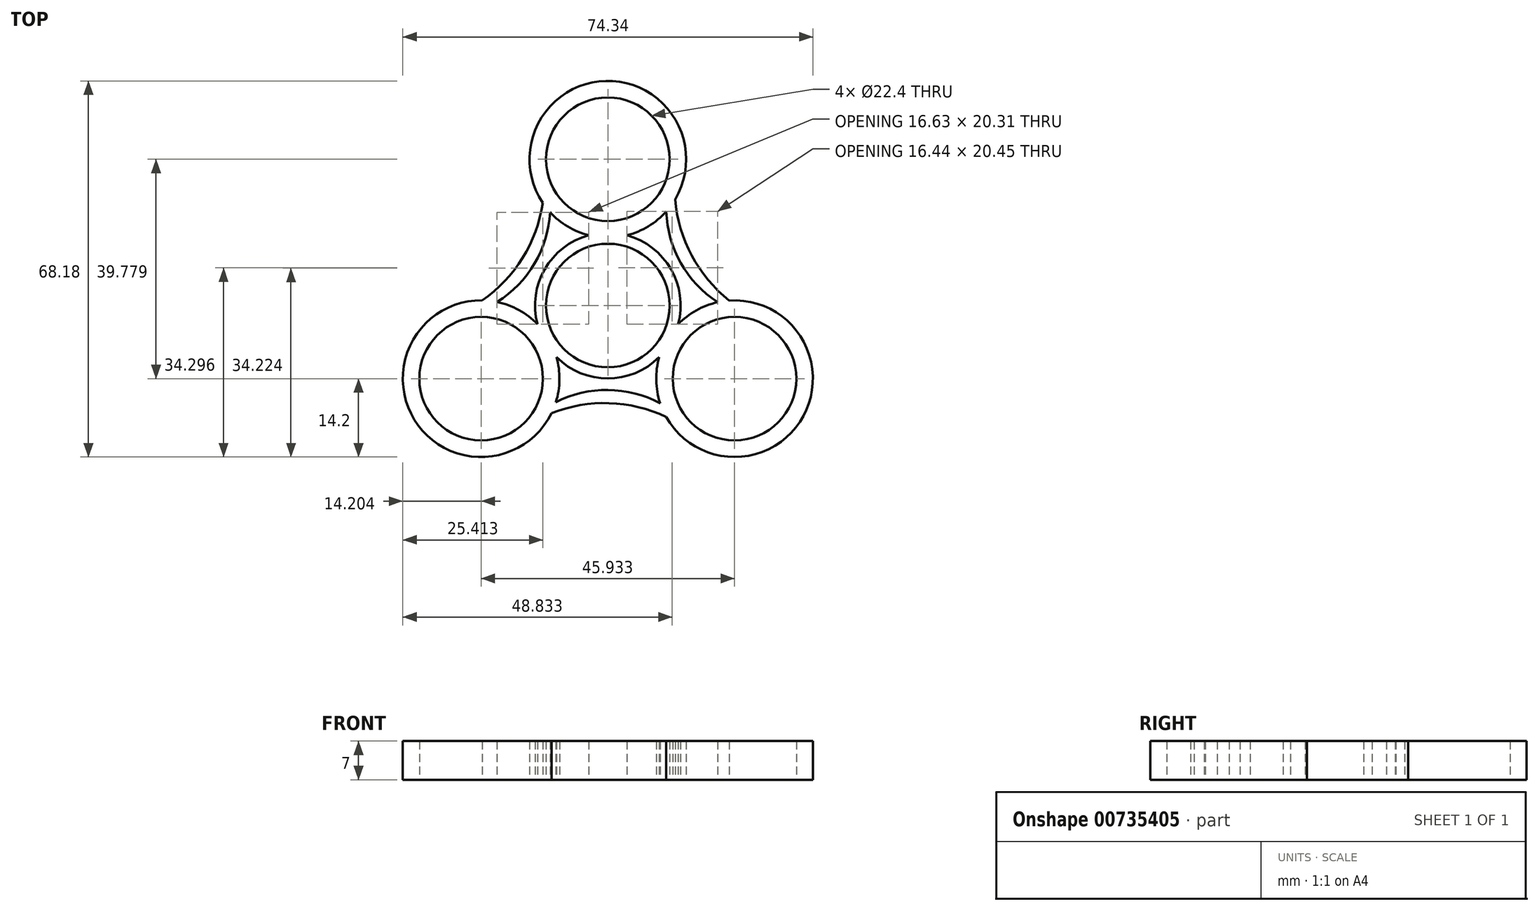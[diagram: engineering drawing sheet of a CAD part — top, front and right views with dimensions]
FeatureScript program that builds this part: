
annotation { "Feature Type Name" : "Feature", "Feature Type Description" : "" }
export const myFeature = defineFeature(function(context is Context, id is Id, definition is map)
    precondition{}
    {
        {
            var Q0;
            Q0=qCreatedBy(makeId("Top.planeOp"),FACE);
            var sketch = newSketch(context, id + "F0", { "sketchPlane" : qUnion([Q0])});
            skCircle(sketch, "E0", {"center": v(0, 0) * mm, "radius": 11.2 * mm});
            skCircle(sketch, "E1", {"center": v(0, 26.52) * mm, "radius": 11.2 * mm});
            skCircle(sketch, "E2.1.0", {"center": v(-22.97, -13.26) * mm, "radius": 11.2 * mm});
            skCircle(sketch, "E2.2.0", {"center": v(22.97, -13.26) * mm, "radius": 11.2 * mm});
            skArc(sketch, "E3", {"start": v(-3.44, 12.74) * mm, "mid": v(-11.43, 6.6) * mm, "end": v(-12.76, -3.39) * mm});
            skArc(sketch, "E4", {"start": v(3.44, 12.74) * mm, "mid": v(0, 40.72) * mm, "end": v(-3.44, 12.74) * mm});
            skArc(sketch, "E5.1.0", {"start": v(-12.76, -3.39) * mm, "mid": v(-35.26, -20.36) * mm, "end": v(-9.31, -9.35) * mm});
            skArc(sketch, "E5.2.0", {"start": v(9.31, -9.35) * mm, "mid": v(35.26, -20.36) * mm, "end": v(12.76, -3.39) * mm});
            skArc(sketch, "E6.trimOffspring", {"start": v(-9.31, -9.35) * mm, "mid": v(0, -13.2) * mm, "end": v(9.31, -9.35) * mm});
            skArc(sketch, "E7.trimOffspring", {"start": v(12.76, -3.39) * mm, "mid": v(11.43, 6.6) * mm, "end": v(3.44, 12.74) * mm});
            skArc(sketch, "E8", {"start": v(-20.07, 0.64) * mm, "mid": v(-13.28, 7.6) * mm, "end": v(-10.46, 16.92) * mm});
            skArc(sketch, "E9", {"start": v(-22.77, 0.94) * mm, "mid": v(-15.44, 8.64) * mm, "end": v(-11.8, 18.62) * mm});
            skArc(sketch, "E10.1.0", {"start": v(10.57, -20.18) * mm, "mid": v(0.24, -17.7) * mm, "end": v(-10.22, -19.53) * mm});
            skArc(sketch, "E10.1.1", {"start": v(9.48, -17.7) * mm, "mid": v(0.05, -15.3) * mm, "end": v(-9.42, -17.52) * mm});
            skArc(sketch, "E10.2.0", {"start": v(12.2, 19.25) * mm, "mid": v(15.2, 9.05) * mm, "end": v(22.02, 0.9) * mm});
            skArc(sketch, "E10.2.1", {"start": v(10.6, 17.06) * mm, "mid": v(13.23, 7.7) * mm, "end": v(19.88, 0.6) * mm});
            skSolve(sketch);
        }
        {
            var Q0;
            Q0=qSketchRegion(id+"F0",true);
            extrude(context, id + "F1", {"entities" : qUnion([Q0]), "depth" : 7 * mm, "offsetDistance" : 25 * mm});
        }
    });
